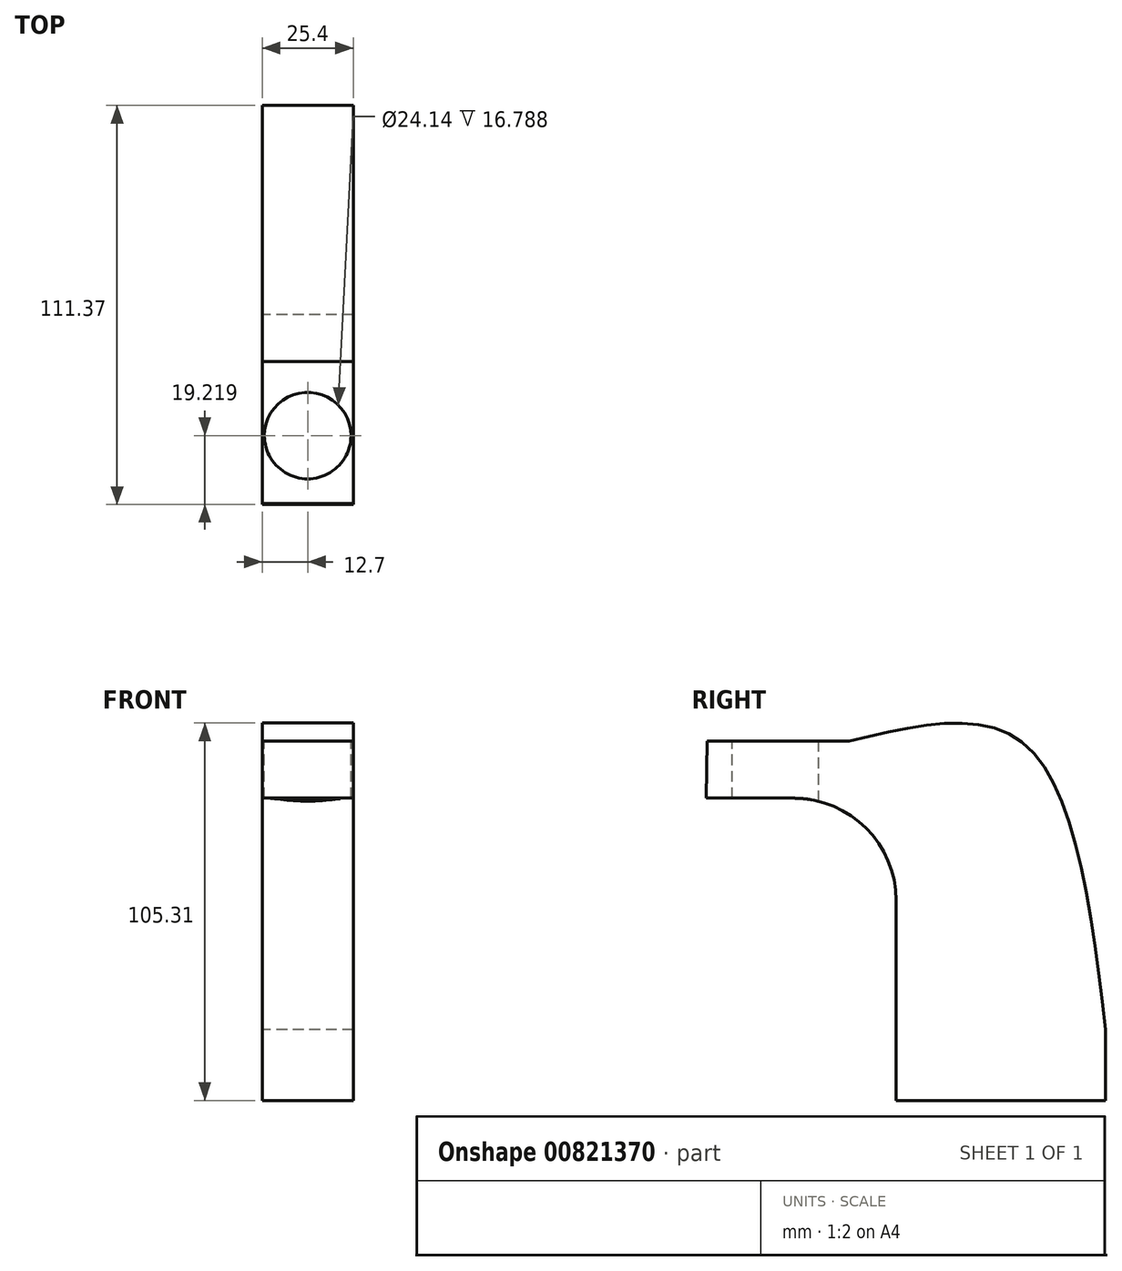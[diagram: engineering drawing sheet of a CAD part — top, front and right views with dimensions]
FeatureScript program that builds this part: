
annotation { "Feature Type Name" : "Feature", "Feature Type Description" : "" }
export const myFeature = defineFeature(function(context is Context, id is Id, definition is map)
    precondition{}
    {
        {
            var Q0;
            Q0=qCreatedBy(makeId("Right.planeOp"),FACE);
            var sketch = newSketch(context, id + "F0", { "sketchPlane" : qUnion([Q0])});
            skLineSegment(sketch, "E0.bottom", {"start": v(15.51, 0) * mm, "end": v(58.41, 0) * mm});
            skLineSegment(sketch, "E0.top", {"start": v(0, -19.74) * mm, "end": v(58.41, -19.74) * mm});
            skLineSegment(sketch, "E0.left", {"start": v(0, 0) * mm, "end": v(0, -19.74) * mm});
            skLineSegment(sketch, "E0.right", {"start": v(58.41, 0) * mm, "end": v(58.41, -19.74) * mm});
            skLineSegment(sketch, "E1.left", {"start": v(0, 0) * mm, "end": v(0, 36.03) * mm});
            skLineSegment(sketch, "E1.right", {"start": v(15.51, 0) * mm, "end": v(15.51, 42.38) * mm});
            skLineSegment(sketch, "E2", {"start": v(15.51, 42.38) * mm, "end": v(15.5, 51.97) * mm});
            skPoint(sketch, "E3.visualSharp", {"position": v(0, 64.6) * mm});
            skArc(sketch, "E3.filletArc", {"start": v(0, 36.03) * mm, "mid": v(-8.37, 56.24) * mm, "end": v(-28.58, 64.6) * mm});
            skPoint(sketch, "E4.visualSharp", {"position": v(15.5, 80.55) * mm});
            skArc(sketch, "E4.filletArc", {"start": v(15.5, 51.97) * mm, "mid": v(7.14, 72.18) * mm, "end": v(-13.07, 80.54) * mm});
            skLineSegment(sketch, "E5", {"start": v(-28.58, 64.6) * mm, "end": v(-52.96, 64.6) * mm});
            skLineSegment(sketch, "E6", {"start": v(-13.07, 80.54) * mm, "end": v(-52.75, 80.54) * mm});
            skLineSegment(sketch, "E7", {"start": v(-52.96, 64.6) * mm, "end": v(-52.75, 80.54) * mm});
            skFitSpline(sketch, "E8", {"points": [v(-13.07, 80.54) * mm, v(34.7, 80.54) * mm, v(58.41, 0) * mm], "startDerivative": vector(126.06, 30.38) * mm, "endDerivative": vector(21.76, -181.58) * mm});
            skSolve(sketch);
        }
        {
            var Q0;
            Q0 = qSketchRegion(id + "F0", true);
            extrude(context, id + "F1", {"entities" : qUnion([Q0]), "depth" : 25.4 * mm, "offsetDistance" : 25.4 * mm});
        }
        {
            var Q0;
            Q0=makeQuery(id+"F1.opExtrude","SWEPT_FACE",FACE,{"disambiguationData":[OSD([sQuery(id+"F0.wireOp",EDGE,"E6")])]});
            var sketch = newSketch(context, id + "F2", { "sketchPlane" : qUnion([Q0])});
            skCircle(sketch, "E9", {"center": v(12.7, -33.73) * mm, "radius": 12.07 * mm});
            skSolve(sketch);
        }
        {
            var Q0;
            Q0=makeQuery(id+"F2.imprint","IMPRINT",FACE,{"disambiguationData":[TD([[makeQuery(id+"F2.imprint","IMPRINT",EDGE,{"derivedFrom":sQuery(id+"F2.wireOp",EDGE,"E9")}),1.0]])]});
            extrude(context, id + "F3", {"entities" : qUnion([Q0]), "operationType" : NewBodyOperationType.REMOVE, "endBound" : BoundingType.THROUGH_ALL, "oppositeDirection" : true, "depth" : 12.2 * mm, "offsetDistance" : 25.4 * mm});
        }
    });
